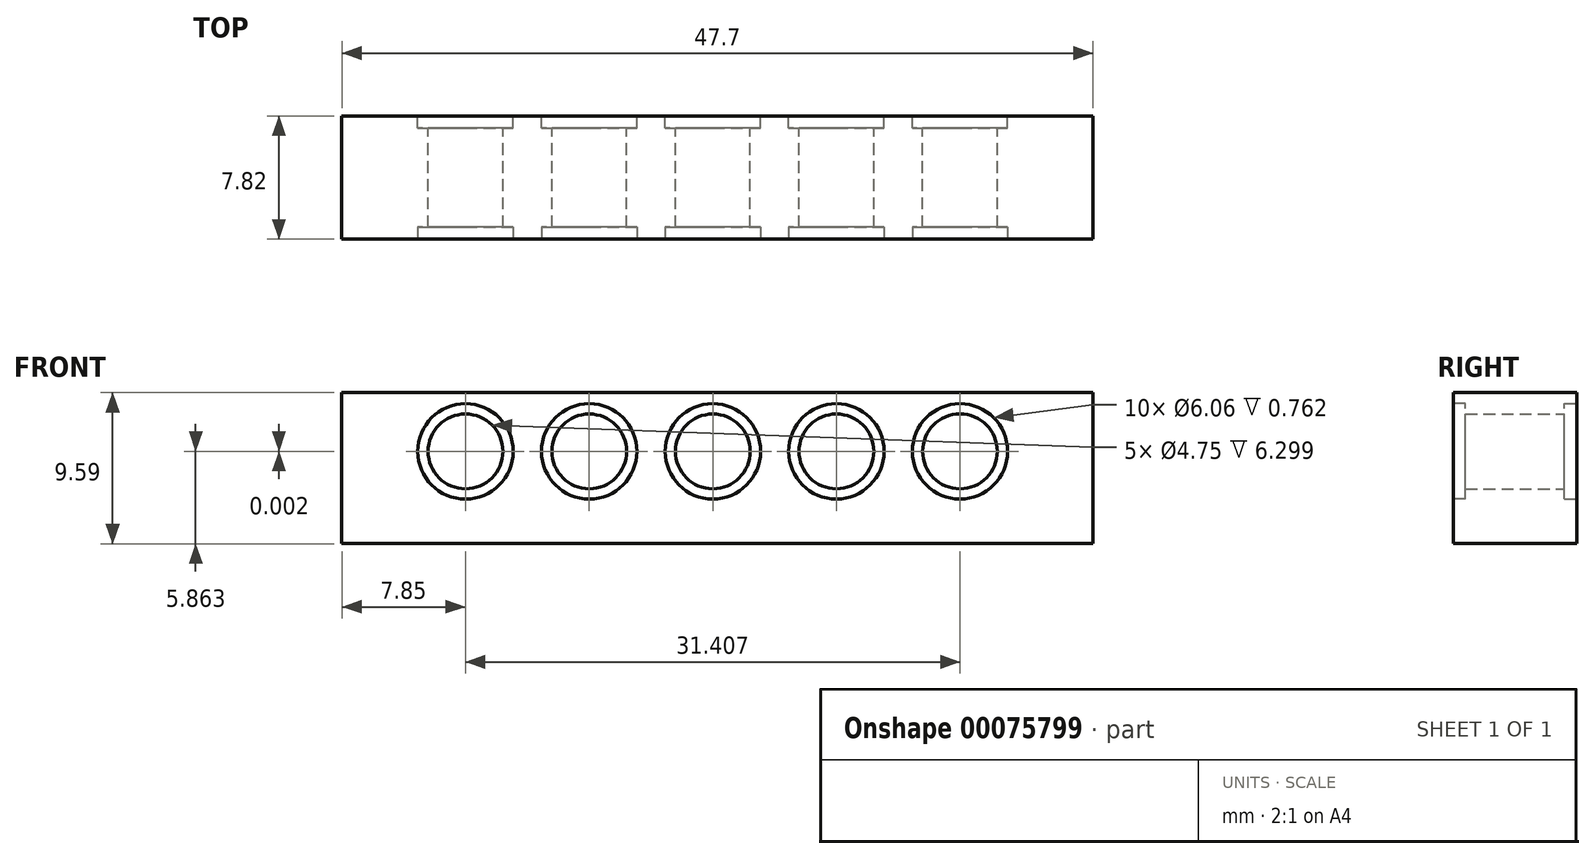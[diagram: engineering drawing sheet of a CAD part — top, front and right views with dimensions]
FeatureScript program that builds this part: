
annotation { "Feature Type Name" : "Feature", "Feature Type Description" : "" }
export const myFeature = defineFeature(function(context is Context, id is Id, definition is map)
    precondition{}
    {
        {
            var Q0;
            Q0=qCreatedBy(makeId("Front.planeOp"),FACE);
            var sketch = newSketch(context, id + "F0", { "sketchPlane" : qUnion([Q0])});
            skLineSegment(sketch, "E0.bottom", {"start": v(-24.51, 1.05) * mm, "end": v(23.19, 1.05) * mm});
            skLineSegment(sketch, "E0.top", {"start": v(-24.51, -8.54) * mm, "end": v(23.19, -8.54) * mm});
            skLineSegment(sketch, "E0.left", {"start": v(-24.51, 1.05) * mm, "end": v(-24.51, -8.54) * mm});
            skLineSegment(sketch, "E0.right", {"start": v(23.19, 1.05) * mm, "end": v(23.19, -8.54) * mm});
            skSolve(sketch);
        }
        {
            var Q0;
            Q0=makeQuery(id+"F0.imprint","IMPRINT",FACE,{"disambiguationData":[TD([[makeQuery(id+"F0.imprint","IMPRINT",EDGE,{"derivedFrom":sQuery(id+"F0.wireOp",EDGE,"E0.bottom")}),-1.0]])]});
            extrude(context, id + "F1", {"entities" : qUnion([Q0]), "depth" : 7.82 * mm});
        }
        {
            var Q0;
            Q0=qCreatedBy(makeId("Front.planeOp"),FACE);
            var sketch = newSketch(context, id + "F2", { "sketchPlane" : qUnion([Q0])});
            skLineSegment(sketch, "E1.0", {"start": v(-24.51, 1.05) * mm, "end": v(23.19, 1.05) * mm});
            skLineSegment(sketch, "E2", {"start": v(-16.66, 1.05) * mm, "end": v(-16.66, 0.35) * mm});
            skLineSegment(sketch, "E3.0", {"start": v(-24.51, 1.05) * mm, "end": v(-24.51, -8.54) * mm});
            skCircle(sketch, "E4", {"center": v(-16.66, -2.68) * mm, "radius": 3.03 * mm});
            skCircle(sketch, "E5", {"center": v(-8.8, -2.68) * mm, "radius": 3.03 * mm});
            skCircle(sketch, "E6", {"center": v(-0.95, -2.68) * mm, "radius": 3.03 * mm});
            skCircle(sketch, "E7", {"center": v(6.9, -2.68) * mm, "radius": 3.03 * mm});
            skCircle(sketch, "E8", {"center": v(14.75, -2.67) * mm, "radius": 3.03 * mm});
            skCircle(sketch, "E9", {"center": v(14.75, -2.67) * mm, "radius": 2.37 * mm});
            skSolve(sketch);
        }
        {
            var Q0;
            Q0=qCreatedBy(makeId("Front.planeOp"),FACE);
            var sketch = newSketch(context, id + "F3", { "sketchPlane" : qUnion([Q0])});
            skCircle(sketch, "E10.0", {"center": v(14.75, -2.67) * mm, "radius": 2.37 * mm});
            skCircle(sketch, "E11.0", {"center": v(6.9, -2.68) * mm, "radius": 2.37 * mm});
            skCircle(sketch, "E12.0", {"center": v(-0.95, -2.68) * mm, "radius": 2.37 * mm});
            skCircle(sketch, "E13.0", {"center": v(-8.8, -2.68) * mm, "radius": 2.37 * mm});
            skCircle(sketch, "E14.0", {"center": v(-16.66, -2.68) * mm, "radius": 2.37 * mm});
            skSolve(sketch);
        }
        {
            var Q0;
            Q0 = qSketchRegion(id + "F3", true);
            extrude(context, id + "F4", {"entities" : qUnion([Q0]), "operationType" : NewBodyOperationType.REMOVE, "depth" : 8.12 * mm});
        }
        {
            var Q0;
            Q0=qCreatedBy(makeId("Front.planeOp"),FACE);
            var sketch = newSketch(context, id + "F5", { "sketchPlane" : qUnion([Q0])});
            skCircle(sketch, "E15.0", {"center": v(14.75, -2.67) * mm, "radius": 3.03 * mm});
            skCircle(sketch, "E15.1", {"center": v(6.9, -2.68) * mm, "radius": 3.03 * mm});
            skCircle(sketch, "E15.2", {"center": v(-0.95, -2.68) * mm, "radius": 3.03 * mm});
            skCircle(sketch, "E15.3", {"center": v(-8.8, -2.68) * mm, "radius": 3.03 * mm});
            skCircle(sketch, "E15.4", {"center": v(-16.66, -2.68) * mm, "radius": 3.03 * mm});
            skSolve(sketch);
        }
        {
            var Q0;
            Q0 = qSketchRegion(id + "F5", true);
            extrude(context, id + "F6", {"entities" : qUnion([Q0]), "operationType" : NewBodyOperationType.REMOVE, "depth" : 0.76 * mm});
        }
        {
            var Q0;
            Q0=makeQuery(id+"F1.opExtrude","CAP_FACE",FACE,{"disambiguationData":[OSD([sQuery(id+"F0.wireOp",EDGE,"E0.bottom"),sQuery(id+"F0.wireOp",EDGE,"E0.top"),sQuery(id+"F0.wireOp",EDGE,"E0.left"),sQuery(id+"F0.wireOp",EDGE,"E0.right")])],"isStart":false});
            var sketch = newSketch(context, id + "F7", { "sketchPlane" : qUnion([Q0])});
            skCircle(sketch, "E16.0", {"center": v(14.75, -2.67) * mm, "radius": 3.03 * mm});
            skCircle(sketch, "E16.1", {"center": v(6.9, -2.68) * mm, "radius": 3.03 * mm});
            skCircle(sketch, "E16.2", {"center": v(-0.95, -2.68) * mm, "radius": 3.03 * mm});
            skCircle(sketch, "E16.3", {"center": v(-8.8, -2.68) * mm, "radius": 3.03 * mm});
            skCircle(sketch, "E16.4", {"center": v(-16.66, -2.68) * mm, "radius": 3.03 * mm});
            skSolve(sketch);
        }
        {
            var Q0;
            Q0 = qSketchRegion(id + "F7", true);
            extrude(context, id + "F8", {"entities" : qUnion([Q0]), "operationType" : NewBodyOperationType.REMOVE, "oppositeDirection" : true, "depth" : 0.76 * mm});
        }
    });
